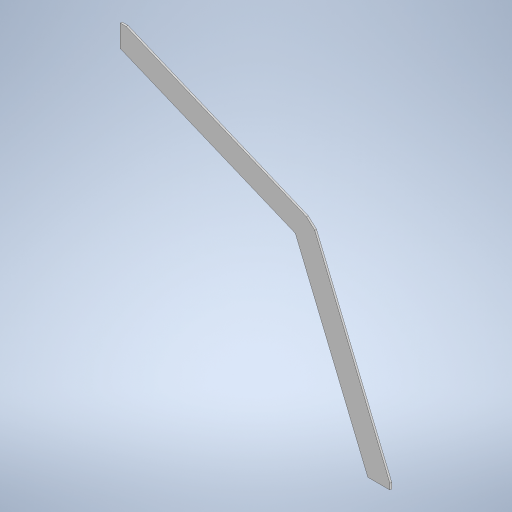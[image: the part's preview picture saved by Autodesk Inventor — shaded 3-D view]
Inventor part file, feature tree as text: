
AUTODESK INVENTOR PART (.ipt)
format: ipt  version: 2024.2 (Build 282272000, 272)  size: 288,256 bytes
history: native  units: mm
features: other x5, sheet_metal_op x1, sketch x1
ambient origin geometry x8: Origin, YZ Plane, XZ Plane, XY Plane, X Axis, Y Axis, Z Axis, Center Point
bodies: Solid1 (feature_tree)
feature tree (7):
  sheet_metal_op  "Face1"
  other  "Corner Chamfer1"
  other  "Corner Chamfer2"
  other  "Corner Chamfer3"
  sketch  "Sketch1"  dims[d6=506.0mm d15=2.0mm d16=25.0mm d17=7.0mm d18=6.0mm d19=22.5deg d20=7.0mm d21=6.0mm d22=22.5deg d23=6.0mm d24=6.0mm d25=4.363323mm]
  other  "Plate1"
  other  "Definition1"
